# Revit family: 756-102-ISI-DN700-2800
name_source: partatom
category: Pipe Accessories
units: mm (PartAtom-declared; Revit-internal decimal feet)

## family parameters
Always vertical = Yes
Cut with Voids When Loaded = No
Part Type = Valve - Breaks Into
Round Connector Dimension = Use Diameter
Shared = No
Work Plane-Based = No

## types (27) — shared parameters
Body_wallthickness = 10 mm  [stored 0.0328084 ft]
DN0700_PN10 = 756-0700-1-04002
DN0700_PN16 = 756-0700-1-14002
DN0800_PN10 = 756-0800-1-04002
DN0800_PN16 = 756-0800-1-14002
DN0900_PN10 = 756-0900-1-04002
DN0900_PN16 = 756-0900-1-14002
DN1000_PN10 = 756-1000-1-04002
DN1000_PN16 = 756-1000-1-14002
DN1200_PN10 = 756-1200-1-04002
DN1200_PN16 = 756-1200-1-14002
DN1400_PN10 = 756-1400-1-04002
DN1400_PN16 = 756-1400-1-14002
DN1500_PN10 = 756-1500-1-04002
DN1500_PN16 = 756-1500-1-14002
DN1600_PN10 = 756-1600-1-04002
DN1600_PN16 = 756-1600-1-14002
DN1800_PN10 = 756-1800-1-04002
DN1800_PN16 = 756-1800-1-14002
DN2000_PN10 = 756-2000-1-04002
DN2000_PN16 = 756-2000-1-14002
DN2200_ PN16 DIN = 756-2200-1-14002
DN2200_PN10 DIN = 756-2200-1-04002
DN2400_ PN10 DIN = 756-2400-1-04002
DN2400_ PN16 DIN = 756-2400-1-14002
DN2600_PN10 = 756-2600-1-04002
DN2600_PN16 = 756-2600-1-14002
DN2800_PN10 = 756-2800-1-04002
Description_ = AVK DOUBLE ECC. BUTTERFLY VALVE, LONG
GB_Flange = 5 mm  [stored 0.0164042 ft]
Offset = 3 mm  [stored 0.00984252 ft]
Pin_dia = 60 mm  [stored 0.19685 ft]
RF_Cut_Thickness = 5 mm  [stored 0.0164042 ft]
Search_table = 756-102-ISI-DN700-2800
URL_product_pages = https://www.avkvalves.com

## per-type parameters (varying)
- DN0700_PN10: A=335 mm; A2=197 mm; B=605 mm; Bottom_Depth=1050 mm; Bottom_width=395 mm; C=255 mm; C_Rod=38 mm  [stored 0.124672 ft]; D1=10 mm  [stored 0.0328084 ft]; DN=700 mm; Disc_Dia=690 mm; Disc_width=40 mm  [stored 0.131234 ft]; Flange_OD=448 mm; Flange_Thickness=40 mm  [stored 0.131234 ft]; GB_Dia=40 mm  [stored 0.131234 ft]; GB_HW=125 mm; GB_HW_2=42 mm  [stored 0.137795 ft]; GB_Ref=17 mm; GB_Width=40 mm  [stored 0.131234 ft]; GB_Width_2=117 mm; GB_Width_3=130 mm; GB_Width_Ref=143 mm; Gear_box_Mount_Flange_width=102 mm; Gear_box_Mount_width=16 mm; Gear_box_depth=300 mm; H1=565 mm; H2=550 mm; ID (Radius)=350 mm; L=430 mm; L1=127 mm; L2=133 mm; Pin_Depth=798 mm; Pin_width=215 mm; Rf_Dia=397 mm; Rib_depth=30 mm  [stored 0.0984252 ft]; Rib_height=407 mm; Rib_height_2=118 mm; Rib_width=350 mm; Rib_width_2=204 mm; T(Addon)=605 mm; W1=448 mm; W2=730 mm; W2_Ref=125 mm; W3=533 mm; W4=543 mm
- DN0700_PN16: A=342 mm; A2=201 mm; B=600 mm; Bottom_Depth=1050 mm; Bottom_width=427 mm; C=297 mm; C_Rod=38 mm  [stored 0.124672 ft]; D1=10 mm  [stored 0.0328084 ft]; DN=700 mm; Disc_Dia=690 mm; Disc_width=40 mm  [stored 0.131234 ft]; Flange_OD=455 mm; Flange_Thickness=40 mm  [stored 0.131234 ft]; GB_Dia=40 mm  [stored 0.131234 ft]; GB_HW=125 mm; GB_HW_2=42 mm  [stored 0.137795 ft]; GB_Ref=17 mm; GB_Width=82 mm; GB_Width_2=117 mm; GB_Width_3=130 mm; GB_Width_Ref=143 mm; Gear_box_Mount_Flange_width=107 mm; Gear_box_Mount_width=17 mm; Gear_box_depth=307 mm; H1=560 mm; H2=565 mm; ID (Radius)=350 mm; L=430 mm; L1=124 mm; L2=130 mm; Pin_Depth=805 mm; Pin_width=215 mm; Rf_Dia=397 mm; Rib_depth=30 mm  [stored 0.0984252 ft]; Rib_height=414 mm; Rib_height_2=105 mm; Rib_width=350 mm; Rib_width_2=214 mm; T(Addon)=600 mm; W1=455 mm; W2=725 mm; W2_Ref=110 mm; W3=527 mm; W4=537 mm
- DN0800_PN10: A=313 mm; A2=184 mm; B=670 mm; Bottom_Depth=1200 mm; Bottom_width=460 mm; C=349 mm; C_Rod=38 mm  [stored 0.124672 ft]; D1=10 mm  [stored 0.0328084 ft]; DN=800 mm; Disc_Dia=789 mm; Disc_width=40 mm  [stored 0.131234 ft]; Flange_OD=508 mm; Flange_Thickness=40 mm  [stored 0.131234 ft]; GB_Dia=41 mm  [stored 0.134514 ft]; GB_HW=155 mm; GB_HW_2=52 mm; GB_Ref=21 mm  [stored 0.0688976 ft]; GB_Width=114 mm; GB_Width_2=126 mm; GB_Width_3=140 mm; GB_Width_Ref=157 mm; Gear_box_Mount_Flange_width=112 mm; Gear_box_Mount_width=17 mm; Gear_box_depth=278 mm; H1=630 mm; H2=620 mm; ID (Radius)=400 mm; L=470 mm; L1=156 mm; L2=162 mm; Pin_Depth=908 mm; Pin_width=235 mm; Rf_Dia=450 mm; Rib_depth=30 mm  [stored 0.0984252 ft]; Rib_height=461 mm; Rib_height_2=122 mm; Rib_width=390 mm; Rib_width_2=223 mm; T(Addon)=670 mm; W1=508 mm; W2=765 mm; W2_Ref=155 mm; W3=627 mm; W4=636 mm
- DN0800_PN16: A=342 mm; A2=201 mm; B=670 mm; Bottom_Depth=1200 mm; Bottom_width=492 mm; C=317 mm; C_Rod=38 mm  [stored 0.124672 ft]; D1=10 mm  [stored 0.0328084 ft]; DN=800 mm; Disc_Dia=789 mm; Disc_width=40 mm  [stored 0.131234 ft]; Flange_OD=513 mm; Flange_Thickness=40 mm  [stored 0.131234 ft]; GB_Dia=41 mm  [stored 0.134514 ft]; GB_HW=155 mm; GB_HW_2=52 mm; GB_Ref=21 mm  [stored 0.0688976 ft]; GB_Width=82 mm; GB_Width_2=126 mm; GB_Width_3=140 mm; GB_Width_Ref=157 mm; Gear_box_Mount_Flange_width=116 mm; Gear_box_Mount_width=18 mm  [stored 0.0590551 ft]; Gear_box_depth=307 mm; H1=630 mm; H2=635 mm; ID (Radius)=400 mm; L=470 mm; L1=155 mm; L2=161 mm; Pin_Depth=913 mm; Pin_width=235 mm; Rf_Dia=450 mm; Rib_depth=30 mm  [stored 0.0984252 ft]; Rib_height=466 mm; Rib_height_2=117 mm; Rib_width=390 mm; Rib_width_2=232 mm; T(Addon)=670 mm; W1=513 mm; W2=795 mm; W2_Ref=155 mm; W3=626 mm; W4=635 mm
- DN0900_PN10: A=342 mm; A2=201 mm; B=740 mm; Bottom_Depth=1350 mm; Bottom_width=524 mm; C=337 mm; C_Rod=38 mm  [stored 0.124672 ft]; D1=10 mm  [stored 0.0328084 ft]; DN=900 mm; Disc_Dia=889 mm; Disc_width=40 mm  [stored 0.131234 ft]; Flange_OD=558 mm; Flange_Thickness=40 mm  [stored 0.131234 ft]; GB_Dia=46 mm  [stored 0.150919 ft]; GB_HW=165 mm; GB_HW_2=55 mm  [stored 0.180446 ft]; GB_Ref=22 mm  [stored 0.0721785 ft]; GB_Width=82 mm; GB_Width_2=140 mm; GB_Width_3=155 mm; GB_Width_Ref=170 mm; Gear_box_Mount_Flange_width=121 mm; Gear_box_Mount_width=19 mm  [stored 0.062336 ft]; Gear_box_depth=307 mm; H1=694 mm; H2=690 mm; ID (Radius)=450 mm; L=510 mm; L1=186 mm; L2=192 mm; Pin_Depth=1008 mm; Pin_width=255 mm; Rf_Dia=500 mm; Rib_depth=30 mm  [stored 0.0984252 ft]; Rib_height=507 mm; Rib_height_2=137 mm; Rib_width=430 mm; Rib_width_2=241 mm; T(Addon)=740 mm; W1=558 mm; W2=865 mm; W2_Ref=175 mm; W3=722 mm; W4=730 mm
- DN0900_PN16: A=313 mm; A2=184 mm; B=740 mm; Bottom_Depth=1350 mm; Bottom_width=556 mm; C=369 mm; C_Rod=38 mm  [stored 0.124672 ft]; D1=10 mm  [stored 0.0328084 ft]; DN=900 mm; Disc_Dia=889 mm; Disc_width=40 mm  [stored 0.131234 ft]; Flange_OD=563 mm; Flange_Thickness=40 mm  [stored 0.131234 ft]; GB_Dia=46 mm  [stored 0.150919 ft]; GB_HW=165 mm; GB_HW_2=55 mm  [stored 0.180446 ft]; GB_Ref=22 mm  [stored 0.0721785 ft]; GB_Width=114 mm; GB_Width_2=140 mm; GB_Width_3=155 mm; GB_Width_Ref=170 mm; Gear_box_Mount_Flange_width=125 mm; Gear_box_Mount_width=19 mm  [stored 0.062336 ft]; Gear_box_depth=278 mm; H1=694 mm; H2=705 mm; ID (Radius)=450 mm; L=510 mm; L1=185 mm; L2=191 mm; Pin_Depth=1013 mm; Pin_width=255 mm; Rf_Dia=500 mm; Rib_depth=30 mm  [stored 0.0984252 ft]; Rib_height=511 mm; Rib_height_2=132 mm; Rib_width=430 mm; Rib_width_2=250 mm; T(Addon)=740 mm; W1=563 mm; W2=835 mm; W2_Ref=175 mm; W3=721 mm; W4=729 mm
- DN1000_PN10: A=469 mm; A2=276 mm; B=836 mm; Bottom_Depth=1500 mm; Bottom_width=588 mm; C=306 mm; C_Rod=48 mm  [stored 0.15748 ft]; D1=10 mm  [stored 0.0328084 ft]; DN=1000 mm; Disc_Dia=988 mm; Disc_width=50 mm  [stored 0.164042 ft]; Flange_OD=615 mm; Flange_Thickness=40 mm  [stored 0.131234 ft]; GB_Dia=55 mm  [stored 0.180446 ft]; GB_HW=210 mm; GB_HW_2=70 mm  [stored 0.229659 ft]; GB_Ref=28 mm  [stored 0.0918635 ft]; GB_Width=31 mm  [stored 0.101706 ft]; GB_Width_2=158 mm; GB_Width_3=175 mm; GB_Width_Ref=183 mm; Gear_box_Mount_Flange_width=130 mm; Gear_box_Mount_width=20 mm  [stored 0.0656168 ft]; Gear_box_depth=434 mm; H1=781 mm; H2=770 mm; ID (Radius)=500 mm; L=550 mm; L1=216 mm; L2=222 mm; Pin_Depth=1115 mm; Pin_width=275 mm; Rf_Dia=556 mm; Rib_depth=40 mm  [stored 0.131234 ft]; Rib_height=559 mm; Rib_height_2=166 mm; Rib_width=470 mm; Rib_width_2=259 mm; T(Addon)=836 mm; W1=615 mm; W2=1040 mm; W2_Ref=204 mm; W3=816 mm; W4=824 mm
- DN1000_PN16: A=469 mm; A2=276 mm; B=837 mm; Bottom_Depth=1500 mm; Bottom_width=620 mm; C=306 mm; C_Rod=48 mm  [stored 0.15748 ft]; D1=10 mm  [stored 0.0328084 ft]; DN=1000 mm; Disc_Dia=988 mm; Disc_width=50 mm  [stored 0.164042 ft]; Flange_OD=628 mm; Flange_Thickness=40 mm  [stored 0.131234 ft]; GB_Dia=55 mm  [stored 0.180446 ft]; GB_HW=210 mm; GB_HW_2=70 mm  [stored 0.229659 ft]; GB_Ref=28 mm  [stored 0.0918635 ft]; GB_Width=31 mm  [stored 0.101706 ft]; GB_Width_2=158 mm; GB_Width_3=175 mm; GB_Width_Ref=183 mm; Gear_box_Mount_Flange_width=134 mm; Gear_box_Mount_width=21 mm  [stored 0.0688976 ft]; Gear_box_depth=434 mm; H1=782 mm; H2=785 mm; ID (Radius)=500 mm; L=550 mm; L1=215 mm; L2=221 mm; Pin_Depth=1128 mm; Pin_width=275 mm; Rf_Dia=556 mm; Rib_depth=40 mm  [stored 0.131234 ft]; Rib_height=570 mm; Rib_height_2=155 mm; Rib_width=470 mm; Rib_width_2=268 mm; T(Addon)=837 mm; W1=628 mm; W2=1041 mm; W2_Ref=204 mm; W3=814 mm; W4=822 mm
- DN1200_PN10: A=469 mm; A2=276 mm; B=930 mm; Bottom_Depth=1800 mm; Bottom_width=653 mm; C=346 mm; C_Rod=48 mm  [stored 0.15748 ft]; D1=10 mm  [stored 0.0328084 ft]; DN=1200 mm; Disc_Dia=1175 mm; Disc_width=50 mm  [stored 0.164042 ft]; Flange_OD=728 mm; Flange_Thickness=40 mm  [stored 0.131234 ft]; GB_Dia=80 mm; GB_HW=225 mm; GB_HW_2=75 mm; GB_Ref=30 mm  [stored 0.0984252 ft]; GB_Width=31 mm  [stored 0.101706 ft]; GB_Width_2=176 mm; GB_Width_3=195 mm; GB_Width_Ref=210 mm; Gear_box_Mount_Flange_width=139 mm; Gear_box_Mount_width=21 mm  [stored 0.0688976 ft]; Gear_box_depth=434 mm; H1=850 mm; H2=855 mm; ID (Radius)=600 mm; L=630 mm; L1=269 mm; L2=275 mm; Pin_Depth=1328 mm; Pin_width=315 mm; Rf_Dia=666 mm; Rib_depth=40 mm  [stored 0.131234 ft]; Rib_height=661 mm; Rib_height_2=123 mm; Rib_width=550 mm; Rib_width_2=277 mm; T(Addon)=905 mm; W1=728 mm; W2=1134 mm; W2_Ref=225 mm; W3=986 mm; W4=993 mm
- DN1200_PN16: A=469 mm; A2=276 mm; B=917 mm; Bottom_Depth=1800 mm; Bottom_width=685 mm; C=346 mm; C_Rod=48 mm  [stored 0.15748 ft]; D1=10 mm  [stored 0.0328084 ft]; DN=1200 mm; Disc_Dia=1175 mm; Disc_width=50 mm  [stored 0.164042 ft]; Flange_OD=743 mm; Flange_Thickness=50 mm  [stored 0.164042 ft]; GB_Dia=75 mm; GB_HW=215 mm; GB_HW_2=72 mm; GB_Ref=29 mm  [stored 0.0951444 ft]; GB_Width=31 mm  [stored 0.101706 ft]; GB_Width_2=176 mm; GB_Width_3=195 mm; GB_Width_Ref=210 mm; Gear_box_Mount_Flange_width=143 mm; Gear_box_Mount_width=22 mm  [stored 0.0721785 ft]; Gear_box_depth=434 mm; H1=842 mm; H2=874 mm; ID (Radius)=600 mm; L=630 mm; L1=268 mm; L2=274 mm; Pin_Depth=1343 mm; Pin_width=315 mm; Rf_Dia=666 mm; Rib_depth=40 mm  [stored 0.131234 ft]; Rib_height=675 mm; Rib_height_2=100 mm; Rib_width=530 mm; Rib_width_2=286 mm; T(Addon)=908 mm; W1=743 mm; W2=1121 mm; W2_Ref=215 mm; W3=985 mm; W4=993 mm
- DN1400_PN10: A=469 mm; A2=276 mm; B=1037 mm; Bottom_Depth=2100 mm; Bottom_width=717 mm; C=386 mm; C_Rod=48 mm  [stored 0.15748 ft]; D1=10 mm  [stored 0.0328084 ft]; DN=1400 mm; Disc_Dia=1382 mm; Disc_width=50 mm  [stored 0.164042 ft]; Flange_OD=838 mm; Flange_Thickness=50 mm  [stored 0.164042 ft]; GB_Dia=75 mm; GB_HW=240 mm; GB_HW_2=80 mm; GB_Ref=32 mm  [stored 0.104987 ft]; GB_Width=31 mm  [stored 0.101706 ft]; GB_Width_2=185 mm; GB_Width_3=206 mm; GB_Width_Ref=237 mm; Gear_box_Mount_Flange_width=148 mm; Gear_box_Mount_width=23 mm  [stored 0.0754593 ft]; Gear_box_depth=434 mm; H1=962 mm; H2=970 mm; ID (Radius)=700 mm; L=710 mm; L1=333 mm; L2=339 mm; Pin_Depth=1538 mm; Pin_width=355 mm; Rf_Dia=763 mm; Rib_depth=40 mm  [stored 0.131234 ft]; Rib_height=761 mm; Rib_height_2=125 mm; Rib_width=610 mm; Rib_width_2=295 mm; T(Addon)=1013 mm; W1=838 mm; W2=1241 mm; W2_Ref=240 mm; W3=1182 mm; W4=1189 mm
- DN1400_PN16: A=505 mm; A2=297 mm; B=1049 mm; Bottom_Depth=2100 mm; Bottom_width=749 mm; C=422 mm; C_Rod=48 mm  [stored 0.15748 ft]; D1=10 mm  [stored 0.0328084 ft]; DN=1400 mm; Disc_Dia=1382 mm; Disc_width=50 mm  [stored 0.164042 ft]; Flange_OD=843 mm; Flange_Thickness=50 mm  [stored 0.164042 ft]; GB_Dia=85 mm; GB_HW=240 mm; GB_HW_2=80 mm; GB_Ref=32 mm  [stored 0.104987 ft]; GB_Width=67 mm  [stored 0.219816 ft]; GB_Width_2=193 mm; GB_Width_3=215 mm; GB_Width_Ref=237 mm; Gear_box_Mount_Flange_width=152 mm; Gear_box_Mount_width=24 mm  [stored 0.0787402 ft]; Gear_box_depth=470 mm; H1=964 mm; H2=970 mm; ID (Radius)=700 mm; L=710 mm; L1=333 mm; L2=339 mm; Pin_Depth=1543 mm; Pin_width=355 mm; Rf_Dia=763 mm; Rib_depth=40 mm  [stored 0.131234 ft]; Rib_height=766 mm; Rib_height_2=122 mm; Rib_width=610 mm; Rib_width_2=304 mm; T(Addon)=1018 mm; W1=843 mm; W2=1253 mm; W2_Ref=240 mm; W3=1182 mm; W4=1189 mm
- DN1500_PN10: A=469 mm; A2=276 mm; B=1137 mm; Bottom_Depth=2250 mm; Bottom_width=781 mm; C=406 mm; C_Rod=48 mm  [stored 0.15748 ft]; D1=10 mm  [stored 0.0328084 ft]; DN=1500 mm; Disc_Dia=1482 mm; Disc_width=50 mm  [stored 0.164042 ft]; Flange_OD=893 mm; Flange_Thickness=50 mm  [stored 0.164042 ft]; GB_Dia=100 mm; GB_HW=275 mm; GB_HW_2=92 mm; GB_Ref=37 mm  [stored 0.121391 ft]; GB_Width=31 mm  [stored 0.101706 ft]; GB_Width_2=201 mm; GB_Width_3=224 mm; GB_Width_Ref=250 mm; Gear_box_Mount_Flange_width=157 mm; Gear_box_Mount_width=24 mm  [stored 0.0787402 ft]; Gear_box_depth=434 mm; H1=1037 mm; H2=1070 mm; ID (Radius)=750 mm; L=750 mm; L1=363 mm; L2=369 mm; Pin_Depth=1643 mm; Pin_width=375 mm; Rf_Dia=818 mm; Rib_depth=40 mm  [stored 0.131234 ft]; Rib_height=811 mm; Rib_height_2=145 mm; Rib_width=650 mm; Rib_width_2=313 mm; T(Addon)=1090 mm; W1=893 mm; W2=1341 mm; W2_Ref=275 mm; W3=1274 mm; W4=1281 mm
- DN1500_PN16: A=505 mm; A2=297 mm; B=1149 mm; Bottom_Depth=2250 mm; Bottom_width=813 mm; C=442 mm; C_Rod=48 mm  [stored 0.15748 ft]; D1=10 mm  [stored 0.0328084 ft]; DN=1500 mm; Disc_Dia=1482 mm; Disc_width=50 mm  [stored 0.164042 ft]; Flange_OD=910 mm; Flange_Thickness=50 mm  [stored 0.164042 ft]; GB_Dia=100 mm; GB_HW=275 mm; GB_HW_2=92 mm; GB_Ref=37 mm  [stored 0.121391 ft]; GB_Width=67 mm  [stored 0.219816 ft]; GB_Width_2=209 mm; GB_Width_3=233 mm; GB_Width_Ref=250 mm; Gear_box_Mount_Flange_width=162 mm; Gear_box_Mount_width=25 mm  [stored 0.082021 ft]; Gear_box_depth=470 mm; H1=1049 mm; H2=1070 mm; ID (Radius)=750 mm; L=750 mm; L1=363 mm; L2=369 mm; Pin_Depth=1660 mm; Pin_width=375 mm; Rf_Dia=818 mm; Rib_depth=40 mm  [stored 0.131234 ft]; Rib_height=827 mm; Rib_height_2=139 mm; Rib_width=650 mm; Rib_width_2=323 mm; T(Addon)=1105 mm; W1=913 mm; W2=1353 mm; W2_Ref=275 mm; W3=1274 mm; W4=1281 mm
- DN1600_PN10: A=505 mm; A2=297 mm; B=1224 mm; Bottom_Depth=2400 mm; Bottom_width=846 mm; C=462 mm; C_Rod=48 mm  [stored 0.15748 ft]; D1=10 mm  [stored 0.0328084 ft]; DN=1600 mm; Disc_Dia=1576 mm; Disc_width=50 mm  [stored 0.164042 ft]; Flange_OD=958 mm; Flange_Thickness=50 mm  [stored 0.164042 ft]; GB_Dia=110 mm; GB_HW=300 mm; GB_HW_2=100 mm; GB_Ref=40 mm  [stored 0.131234 ft]; GB_Width=67 mm  [stored 0.219816 ft]; GB_Width_2=217 mm; GB_Width_3=241 mm; GB_Width_Ref=263 mm; Gear_box_Mount_Flange_width=166 mm; Gear_box_Mount_width=26 mm; Gear_box_depth=470 mm; H1=1114 mm; H2=1145 mm; ID (Radius)=800 mm; L=790 mm; L1=390 mm; L2=396 mm; Pin_Depth=1758 mm; Pin_width=395 mm; Rf_Dia=875 mm; Rib_depth=40 mm  [stored 0.131234 ft]; Rib_height=870 mm; Rib_height_2=157 mm; Rib_width=690 mm; Rib_width_2=332 mm; T(Addon)=1180 mm; W1=958 mm; W2=1428 mm; W2_Ref=300 mm; W3=1359 mm; W4=1366 mm
- DN1600_PN16: A=505 mm; A2=297 mm; B=1224 mm; Bottom_Depth=2400 mm; Bottom_width=878 mm; C=462 mm; C_Rod=48 mm  [stored 0.15748 ft]; D1=10 mm  [stored 0.0328084 ft]; DN=1600 mm; Disc_Dia=1576 mm; Disc_width=50 mm  [stored 0.164042 ft]; Flange_OD=965 mm; Flange_Thickness=60 mm  [stored 0.19685 ft]; GB_Dia=110 mm; GB_HW=300 mm; GB_HW_2=100 mm; GB_Ref=40 mm  [stored 0.131234 ft]; GB_Width=67 mm  [stored 0.219816 ft]; GB_Width_2=225 mm; GB_Width_3=250 mm; GB_Width_Ref=263 mm; Gear_box_Mount_Flange_width=171 mm; Gear_box_Mount_width=26 mm; Gear_box_depth=470 mm; H1=1114 mm; H2=1145 mm; ID (Radius)=800 mm; L=790 mm; L1=390 mm; L2=396 mm; Pin_Depth=1765 mm; Pin_width=395 mm; Rf_Dia=875 mm; Rib_depth=40 mm  [stored 0.131234 ft]; Rib_height=877 mm; Rib_height_2=149 mm; Rib_width=670 mm; Rib_width_2=341 mm; T(Addon)=1180 mm; W1=965 mm; W2=1428 mm; W2_Ref=300 mm; W3=1359 mm; W4=1366 mm
- DN1800_PN10: A=605 mm; A2=356 mm; B=1299 mm; Bottom_Depth=2700 mm; Bottom_width=910 mm; C=714 mm; C_Rod=48 mm  [stored 0.15748 ft]; D1=10 mm  [stored 0.0328084 ft]; DN=1800 mm; Disc_Dia=1772 mm; Disc_width=50 mm  [stored 0.164042 ft]; Flange_OD=1058 mm; Flange_Thickness=60 mm  [stored 0.19685 ft]; GB_Dia=80 mm; GB_HW=285 mm; GB_HW_2=95 mm; GB_Ref=38 mm  [stored 0.124672 ft]; GB_Width=279 mm; GB_Width_2=233 mm; GB_Width_3=259 mm; GB_Width_Ref=290 mm; Gear_box_Mount_Flange_width=175 mm; Gear_box_Mount_width=27 mm; Gear_box_depth=570 mm; H1=1219 mm; H2=1220 mm; ID (Radius)=900 mm; L=870 mm; L1=448 mm; L2=454 mm; Pin_Depth=1958 mm; Pin_width=435 mm; Rf_Dia=973 mm; Rib_depth=40 mm  [stored 0.131234 ft]; Rib_height=961 mm; Rib_height_2=162 mm; Rib_width=750 mm; Rib_width_2=350 mm; T(Addon)=1299 mm; W1=1058 mm; W2=1490 mm; W2_Ref=285 mm; W3=1540 mm; W4=1547 mm
- DN1800_PN16: A=605 mm; A2=356 mm; B=1299 mm; Bottom_Depth=2700 mm; Bottom_width=942 mm; C=714 mm; C_Rod=48 mm  [stored 0.15748 ft]; D1=10 mm  [stored 0.0328084 ft]; DN=1800 mm; Disc_Dia=1772 mm; Disc_width=50 mm  [stored 0.164042 ft]; Flange_OD=1065 mm; Flange_Thickness=60 mm  [stored 0.19685 ft]; GB_Dia=80 mm; GB_HW=280 mm; GB_HW_2=93 mm; GB_Ref=37 mm  [stored 0.121391 ft]; GB_Width=279 mm; GB_Width_2=241 mm; GB_Width_3=268 mm; GB_Width_Ref=290 mm; Gear_box_Mount_Flange_width=180 mm; Gear_box_Mount_width=28 mm  [stored 0.0918635 ft]; Gear_box_depth=570 mm; H1=1219 mm; H2=1220 mm; ID (Radius)=900 mm; L=870 mm; L1=448 mm; L2=454 mm; Pin_Depth=1965 mm; Pin_width=435 mm; Rf_Dia=973 mm; Rib_depth=40 mm  [stored 0.131234 ft]; Rib_height=968 mm; Rib_height_2=154 mm; Rib_width=750 mm; Rib_width_2=359 mm; T(Addon)=1299 mm; W1=1065 mm; W2=1490 mm; W2_Ref=280 mm; W3=1540 mm; W4=1547 mm
- DN2000_PN10: A=605 mm; A2=356 mm; B=1462 mm; Bottom_Depth=3000 mm; Bottom_width=974 mm; C=753 mm; C_Rod=48 mm  [stored 0.15748 ft]; D1=10 mm  [stored 0.0328084 ft]; DN=2000 mm; Disc_Dia=1998 mm; Disc_width=50 mm  [stored 0.164042 ft]; Flange_OD=1163 mm; Flange_Thickness=60 mm  [stored 0.19685 ft]; GB_Dia=85 mm; GB_HW=320 mm; GB_HW_2=107 mm; GB_Ref=43 mm  [stored 0.141076 ft]; GB_Width=278 mm; GB_Width_2=249 mm; GB_Width_3=277 mm; GB_Width_Ref=317 mm; Gear_box_Mount_Flange_width=184 mm; Gear_box_Mount_width=28 mm  [stored 0.0918635 ft]; Gear_box_depth=570 mm; H1=1377 mm; H2=1382 mm; ID (Radius)=1000 mm; L=950 mm; L1=521 mm; L2=527 mm; Pin_Depth=2163 mm; Pin_width=475 mm; Rf_Dia=1114 mm; Rib_depth=40 mm  [stored 0.131234 ft]; Rib_height=1057 mm; Rib_height_2=215 mm; Rib_width=830 mm; Rib_width_2=368 mm; T(Addon)=1462 mm; W1=1180 mm; W2=1653 mm; W2_Ref=320 mm; W3=1753 mm; W4=1760 mm
- DN2000_PN16: A=605 mm; A2=356 mm; B=1461 mm; Bottom_Depth=3000 mm; Bottom_width=1006 mm; C=754 mm; C_Rod=48 mm  [stored 0.15748 ft]; D1=10 mm  [stored 0.0328084 ft]; DN=2000 mm; Disc_Dia=1998 mm; Disc_width=50 mm  [stored 0.164042 ft]; Flange_OD=1173 mm; Flange_Thickness=60 mm  [stored 0.19685 ft]; GB_Dia=85 mm; GB_HW=320 mm; GB_HW_2=107 mm; GB_Ref=43 mm  [stored 0.141076 ft]; GB_Width=279 mm; GB_Width_2=257 mm; GB_Width_3=285 mm; GB_Width_Ref=317 mm; Gear_box_Mount_Flange_width=189 mm; Gear_box_Mount_width=29 mm  [stored 0.0951444 ft]; Gear_box_depth=570 mm; H1=1376 mm; H2=1382 mm; ID (Radius)=1000 mm; L=950 mm; L1=521 mm; L2=527 mm; Pin_Depth=2173 mm; Pin_width=475 mm; Rf_Dia=1114 mm; Rib_depth=40 mm  [stored 0.131234 ft]; Rib_height=1066 mm; Rib_height_2=204 mm; Rib_width=830 mm; Rib_width_2=377 mm; T(Addon)=1461 mm; W1=1180 mm; W2=1652 mm; W2_Ref=320 mm; W3=1753 mm; W4=1760 mm
- DN2200_PN10 DIN: A=634 mm; A2=373 mm; B=1551 mm; Bottom_Depth=3300 mm; Bottom_width=1000 mm; C=858 mm; C_Rod=48 mm  [stored 0.15748 ft]; D1=10 mm  [stored 0.0328084 ft]; DN=2200 mm; Disc_Dia=2187 mm; Disc_width=50 mm  [stored 0.164042 ft]; Flange_OD=1278 mm; Flange_Thickness=60 mm  [stored 0.19685 ft]; GB_Dia=90 mm; GB_HW=350 mm; GB_HW_2=117 mm; GB_Ref=47 mm  [stored 0.154199 ft]; GB_Width=343 mm; GB_Width_2=273 mm; GB_Width_3=303 mm; GB_Width_Ref=343 mm; Gear_box_Mount_Flange_width=198 mm; Gear_box_Mount_width=30 mm  [stored 0.0984252 ft]; Gear_box_depth=599 mm; H1=1461 mm; H2=1482 mm; ID (Radius)=1100 mm; L=1030 mm; L1=576 mm; L2=582 mm; Pin_Depth=2378 mm; Pin_width=515 mm; Rf_Dia=1180 mm; Rib_depth=40 mm  [stored 0.131234 ft]; Rib_height=1161 mm; Rib_height_2=184 mm; Rib_width=910 mm; Rib_width_2=395 mm; T(Addon)=1566 mm; W1=1278 mm; W2=1742 mm; W2_Ref=325 mm; W3=1926 mm; W4=1932 mm
- DN2200_ PN16 DIN: A=605 mm; A2=356 mm; B=1540 mm; Bottom_Depth=3300 mm; Bottom_width=1000 mm; C=794 mm; C_Rod=48 mm  [stored 0.15748 ft]; D1=10 mm  [stored 0.0328084 ft]; DN=2200 mm; Disc_Dia=2187 mm; Disc_width=50 mm  [stored 0.164042 ft]; Flange_OD=1275 mm; Flange_Thickness=60 mm  [stored 0.19685 ft]; GB_Dia=90 mm; GB_HW=350 mm; GB_HW_2=117 mm; GB_Ref=47 mm  [stored 0.154199 ft]; GB_Width=279 mm; GB_Width_2=265 mm; GB_Width_3=294 mm; GB_Width_Ref=343 mm; Gear_box_Mount_Flange_width=193 mm; Gear_box_Mount_width=30 mm  [stored 0.0984252 ft]; Gear_box_depth=570 mm; H1=1450 mm; H2=1472 mm; ID (Radius)=1100 mm; L=1030 mm; L1=576 mm; L2=582 mm; Pin_Depth=2375 mm; Pin_width=515 mm; Rf_Dia=1180 mm; Rib_depth=40 mm  [stored 0.131234 ft]; Rib_height=1159 mm; Rib_height_2=175 mm; Rib_width=910 mm; Rib_width_2=386 mm; T(Addon)=1540 mm; W1=1275 mm; W2=1731 mm; W2_Ref=325 mm; W3=1926 mm; W4=1932 mm
- DN2400_ PN10 DIN: A=648 mm; A2=381 mm; B=1668 mm; Bottom_Depth=3600 mm; Bottom_width=1103 mm; C=877 mm; C_Rod=48 mm  [stored 0.15748 ft]; D1=10 mm  [stored 0.0328084 ft]; DN=2400 mm; Disc_Dia=2382 mm; Disc_width=50 mm  [stored 0.164042 ft]; Flange_OD=1380 mm; Flange_Thickness=70 mm  [stored 0.229659 ft]; GB_Dia=100 mm; GB_HW=345 mm; GB_HW_2=115 mm; GB_Ref=46 mm  [stored 0.150919 ft]; GB_Width=322 mm; GB_Width_2=280 mm; GB_Width_3=312 mm; GB_Width_Ref=370 mm; Gear_box_Mount_Flange_width=202 mm; Gear_box_Mount_width=31 mm  [stored 0.101706 ft]; Gear_box_depth=613 mm; H1=1568 mm; H2=1613 mm; ID (Radius)=1200 mm; L=1110 mm; L1=633 mm; L2=639 mm; Pin_Depth=2580 mm; Pin_width=555 mm; Rf_Dia=1273 mm; Rib_depth=40 mm  [stored 0.131234 ft]; Rib_height=1255 mm; Rib_height_2=188 mm; Rib_width=970 mm; Rib_width_2=404 mm; T(Addon)=1668 mm; W1=1380 mm; W2=1859 mm; W2_Ref=345 mm; W3=2103 mm; W4=2019 mm
- DN2400_ PN16 DIN: A=786 mm; A2=462 mm; B=1668 mm; Bottom_Depth=3600 mm; Bottom_width=1135 mm; C=732 mm; C_Rod=48 mm  [stored 0.15748 ft]; D1=15 mm  [stored 0.0492126 ft]; DN=2400 mm; Disc_Dia=2381 mm; Disc_width=50 mm  [stored 0.164042 ft]; Flange_OD=1383 mm; Flange_Thickness=70 mm  [stored 0.229659 ft]; GB_Dia=130 mm; GB_HW=345 mm; GB_HW_2=115 mm; GB_Ref=46 mm  [stored 0.150919 ft]; GB_Width=177 mm; GB_Width_2=288 mm; GB_Width_3=321 mm; GB_Width_Ref=370 mm; Gear_box_Mount_Flange_width=207 mm; Gear_box_Mount_width=32 mm  [stored 0.104987 ft]; Gear_box_depth=751 mm; H1=1538 mm; H2=1584 mm; ID (Radius)=1200 mm; L=1110 mm; L1=676 mm; L2=682 mm; Pin_Depth=2583 mm; Pin_width=555 mm; Rf_Dia=1273 mm; Rib_depth=40 mm  [stored 0.131234 ft]; Rib_height=1257 mm; Rib_height_2=156 mm; Rib_width=970 mm; Rib_width_2=413 mm; T(Addon)=1610 mm; W1=1382 mm; W2=1859 mm; W2_Ref=345 mm; W3=2126 mm; W4=2132 mm
- DN2600_PN10: A=635 mm; A2=374 mm; B=1861 mm; Bottom_Depth=3900 mm; Bottom_width=1167 mm; C=879 mm; C_Rod=48 mm  [stored 0.15748 ft]; D1=10 mm  [stored 0.0328084 ft]; DN=2600 mm; Disc_Dia=2582 mm; Disc_width=50 mm  [stored 0.164042 ft]; Flange_OD=1480 mm; Flange_Thickness=70 mm  [stored 0.229659 ft]; GB_Dia=250 mm; GB_HW=400 mm; GB_HW_2=133 mm; GB_Ref=53 mm  [stored 0.173885 ft]; GB_Width=284 mm; GB_Width_2=296 mm; GB_Width_3=329 mm; GB_Width_Ref=230 mm; Gear_box_Mount_Flange_width=211 mm; Gear_box_Mount_width=32 mm  [stored 0.104987 ft]; Gear_box_depth=600 mm; H1=1611 mm; H2=1820 mm; ID (Radius)=1300 mm; L=1190 mm; L1=693 mm; L2=699 mm; Pin_Depth=2780 mm; Pin_width=595 mm; Rf_Dia=1415 mm; Rib_depth=40 mm  [stored 0.131234 ft]; Rib_height=1345 mm; Rib_height_2=131 mm; Rib_width=1050 mm; Rib_width_2=422 mm; T(Addon)=1701 mm; W1=1490 mm; W2=2066 mm; W2_Ref=400 mm; W3=2289 mm; W4=2295 mm
- DN2600_PN16: A=790 mm; A2=465 mm; B=1920 mm; Bottom_Depth=3900 mm; Bottom_width=1199 mm; C=920 mm; C_Rod=48 mm  [stored 0.15748 ft]; D1=15 mm  [stored 0.0492126 ft]; DN=2600 mm; Disc_Dia=2582 mm; Disc_width=50 mm  [stored 0.164042 ft]; Flange_OD=1524 mm; Flange_Thickness=70 mm  [stored 0.229659 ft]; GB_Dia=250 mm; GB_HW=400 mm; GB_HW_2=133 mm; GB_Ref=53 mm  [stored 0.173885 ft]; GB_Width=325 mm; GB_Width_2=304 mm; GB_Width_3=338 mm; GB_Width_Ref=230 mm; Gear_box_Mount_Flange_width=216 mm; Gear_box_Mount_width=33 mm  [stored 0.108268 ft]; Gear_box_depth=755 mm; H1=1670 mm; H2=1855 mm; ID (Radius)=1300 mm; L=1190 mm; L1=693 mm; L2=699 mm; Pin_Depth=2824 mm; Pin_width=595 mm; Rf_Dia=1415 mm; Rib_depth=40 mm  [stored 0.131234 ft]; Rib_height=1385 mm; Rib_height_2=146 mm; Rib_width=1050 mm; Rib_width_2=432 mm; T(Addon)=1750 mm; W1=1535 mm; W2=2120 mm; W2_Ref=400 mm; W3=2289 mm; W4=2295 mm
- DN2800_PN10: A=648 mm; A2=381 mm; B=1973 mm; Bottom_Depth=4200 mm; Bottom_width=1232 mm; C=957 mm; C_Rod=48 mm  [stored 0.15748 ft]; D1=10 mm  [stored 0.0328084 ft]; DN=2800 mm; Disc_Dia=2752 mm; Disc_width=50 mm  [stored 0.164042 ft]; Flange_OD=1590 mm; Flange_Thickness=70 mm  [stored 0.229659 ft]; GB_Dia=215 mm; GB_HW=385 mm; GB_HW_2=128 mm; GB_Ref=51 mm  [stored 0.167323 ft]; GB_Width=322 mm; GB_Width_2=312 mm; GB_Width_3=347 mm; GB_Width_Ref=230 mm; Gear_box_Mount_Flange_width=221 mm; Gear_box_Mount_width=34 mm  [stored 0.111549 ft]; Gear_box_depth=613 mm; H1=1758 mm; H2=1921 mm; ID (Radius)=1400 mm; L=1270 mm; L1=738 mm; L2=739 mm; Pin_Depth=2990 mm; Pin_width=635 mm; Rf_Dia=1500 mm; Rib_depth=40 mm  [stored 0.131234 ft]; Rib_height=1445 mm; Rib_height_2=168 mm; Rib_width=1130 mm; Rib_width_2=441 mm; T(Addon)=1830 mm; W1=1600 mm; W2=2164 mm; W2_Ref=385 mm; W3=2441 mm; W4=2442 mm

note: [stored X ft] marks values corroborated as IEEE doubles in the binary element streams (Revit-internal decimal feet)

## geometry (parser evidence)
native form markers: Sweep x5
no freeform markers — native parametric forms only
